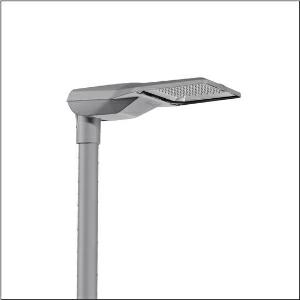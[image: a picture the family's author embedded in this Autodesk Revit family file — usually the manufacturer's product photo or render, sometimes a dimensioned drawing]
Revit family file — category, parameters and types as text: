
# Revit family: streetlight_sl_21_midi___st1_0a_5xe7d43a08lb_da8d
name_source: partatom
category: Lighting Fixtures
units: mm (PartAtom-declared; Revit-internal decimal feet)

## family parameters
Cut with Voids When Loaded = No
Host = Face
Light Source = No
Part Type = Normal
Room Calculation Point = No
Round Connector Dimension = Use Diameter
Shared = No

## types (1)
- --- (1 x LED, 14950 lm, 98.3 W, 4000K)
    Apparent Load = 98 VA
    CIE Flux Codes = 37 72 97 100 100
    Color Rendering = 70
    Color Temperature = 4000K
    Default Elevation = 1800 mm
    Description = Streetlight SL 21 midi, mast luminaire, primary light control with lens, of PMMA, primary optical cover: cover, of toughened safety glass, transparent, light distribution: ST1.0a, light emission: direct distribution, primary light characteristic: asymmetric, installation type: post-top, side-entry, LED, 3G 1.5mm², High Power LED, rated luminous flux: 14.950lm, luminous efficacy: 152lm/W, light colour: 740, colour temperature: 4000K, control: overheat protection, constant luminous flux control, time-dependent luminous flux control, flexible luminous flux parameterisation, mains connection: 220..240V, AC, 50/60Hz, connection cable pre-assembled, cable length: 10,5m, wiring characteristics: H07RN-F, start of lifetime: 98W, end of service life: 101W, reduction: 45W, luminaire housing, of diecast aluminium, powder-coated, Siteco® metallic grey (DB 702S), corrosivity category C5 mid according to DIN EN ISO 12944, please order mast flange separately, inclination adjustable: 0°, 5°, 10°, 15°, sealing non-destructively replaceable, multi-level sealing system, length: 644mm, width: 335mm, height: 110mm, mast flange for spigot size: 42mm (side-entry): 5XC10008XM4, 60/48mm (side-entry/post-top): 5XC10108XM2, 76/60mm (side-entry/post-top): 5XC10108XM1, protection rating (complete): IP66, insulation class (complete): insulation class II (safety insulation), certification: CE, ENEC, ENEC+, VDE, impact resistance: IK09, permissible operating ambient temperature for outdoor applications: -40..+50°C, standard-compliant lighting for roads and squares, packaging unit: 1 piece

Light Distribution: ST1.0a
    Height = 111 mm
    Lamp = 1 x LED
    Lamp Light Flux = 14950 lm
    Lamp Power = 98.3 W
    Lamp count = 1
    Length = 644 mm
    Luminous efficacy = 152 lm/W
    Manufacturer = Siteco
    ModVariant = No
    Model = 5XE7D43A08LB
    Number of Poles = 1
    OnlyDefault = Yes
    Power Factor = 1
    Product Name = Streetlight SL 21 midi | ST1.0a
    Product group = mast luminaire | pylon top
    ProductGroupID = 6100
    Protection Class = Protection class II
    Protection Degree = IP 66
    RLX_Detail_Level = 1
    RLX_Emergency_Light_Flux = 0 lm
    RLX_Emergency_Type = 0
    RLX_Emergency_Type_DB = No
    RlxData = <blob elided: 90233 chars, md5=aaeadba9>
    Socket = socket
    Standby Power = 0 W
    System Light Flux = 14950 lm
    System Power = 98 W
    Type Comments = factory setting: luminous flux: 100 % | Output Level: 100 % | 1020 mA
    Type Image = l_1004298.jpg
    URL = http://relux.com
    VarID = @adj_141167
    Voltage = 0 V
    Weight = 0.00 kg
    Width = 336 mm

## geometry (parser evidence)
native form markers: Blend x4, Sweep x10
no freeform markers — native parametric forms only
